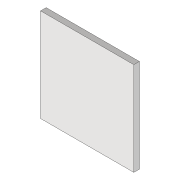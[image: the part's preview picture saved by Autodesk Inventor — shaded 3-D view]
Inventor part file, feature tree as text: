
AUTODESK INVENTOR PART (.ipt)
format: ipt  version: 2020 (Build 240168000, 168)  size: 73,216 bytes
history: native  units: mm
features: extrude x1, sketch x1
ambient origin geometry x8: Origin, YZ Plane, XZ Plane, XY Plane, X Axis, Y Axis, Z Axis, Center Point
bodies: Volumenkörper1 (feature_tree)
feature tree (2):
  extrude  "Extrusion1"  Depth=50.0mm
  sketch  "Skizze1"  dims[d0=50.0mm d1=50.0mm d2=3.0mm d3=0.0mm]
